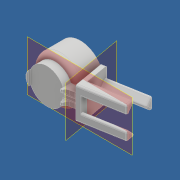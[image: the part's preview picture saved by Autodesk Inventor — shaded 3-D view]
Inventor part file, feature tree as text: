
AUTODESK INVENTOR PART (.ipt)
format: ipt  version: 2017 (Build 210142000, 142)  size: 999,424 bytes
history: native  units: mm
features: fillet x50, sketch x17, extrude x15, projected_geometry x11, chamfer x10, revolve x2, thicken_offset x2, plane x2
ambient origin geometry x8: Origin, YZ Plane, XZ Plane, XY Plane, X Axis, Y Axis, Z Axis, Center Point
bodies: Solid1 (feature_tree)
feature tree (109):
  revolve  "Revolution1"  [1 undecoded]
  extrude  "Extrusion1"  Depth=2.489174mm
  extrude  "Extrusion2"  Depth=5.0mm
  extrude  "Extrusion3"  Depth=1.5mm
  extrude  "Extrusion4"  Depth=1.5mm
  extrude  "Extrusion5"  Depth=1.5mm
  chamfer  "Chamfer1"  Distance=5.0mm
  chamfer  "Chamfer2"  Distance=82.0mm
  chamfer  "Chamfer3"  Distance=82.0mm
  chamfer  "Chamfer4"  Distance=10.0mm
  chamfer  "Chamfer5"  Distance=1.5mm
  chamfer  "Chamfer6"  Angle=45.0deg  [1 undecoded]
  chamfer  "Chamfer9"  Distance=14.6mm
  chamfer  "Chamfer10"  Distance=14.6mm
  chamfer  "Chamfer11"  Distance=7.25mm
  chamfer  "Chamfer12"  Distance=8.0mm Angle=45.0deg
  fillet  "Fillet1"  Radius=8.0mm
  fillet  "Fillet2"  Radius=8.0mm
  fillet  "Fillet3"  Radius=8.0mm
  fillet  "Fillet4"  Radius=5.0mm
  fillet  "Fillet5"  Radius=5.0mm
  fillet  "Fillet6"  Radius=5.0mm
  fillet  "Fillet7"  Radius=5.0mm
  fillet  "Fillet8"  Radius=5.0mm
  fillet  "Fillet11"  Radius=5.0mm
  fillet  "Fillet12"  Radius=2.0mm
  fillet  "Fillet13"  Radius=10.0mm
  fillet  "Fillet14"  Radius=1.0mm
  fillet  "Fillet15"  Radius=1.0mm
  fillet  "Fillet16"  Radius=1.0mm
  fillet  "Fillet17"  Radius=1.0mm
  fillet  "Fillet26"  Radius=1.0mm
  fillet  "Fillet30"  Radius=1.0mm
  extrude  "Extrusion7"  Depth=10.0mm
  extrude  "Extrusion8"  Depth=10.0mm
  fillet  "Fillet34"  Radius=10.0mm
  fillet  "Fillet35"  Radius=3.0mm
  revolve  "Revolution2"  [1 undecoded]
  extrude  "Extrusion9"  Depth=4.0mm
  extrude  "Extrusion10"  Depth=4.0mm
  fillet  "Fillet36"  Radius=1.0mm
  fillet  "Fillet37"  Radius=10.0mm
  extrude  "Extrusion11"  Depth=4.0mm TaperAngle=0.0deg
  extrude  "Extrusion12"  Depth=4.0mm
  extrude  "Extrusion14"  Depth=4.0mm
  extrude  "Extrusion15"  Depth=4.0mm
  thicken_offset  "Thicken1"
  thicken_offset  "Thicken2"
  fillet  "Fillet43"  Radius=5.0mm
  fillet  "Fillet44"  Radius=5.0mm
  fillet  "Fillet45"  Radius=5.0mm
  fillet  "Fillet46"  Radius=5.0mm
  extrude  "Extrusion16"  Depth=4.0mm
  fillet  "Fillet47"  Radius=1.745329mm
  fillet  "Fillet48"  Radius=30.0mm
  fillet  "Fillet49"  Radius=4.75mm
  fillet  "Fillet50"  Radius=10.0mm
  fillet  "Fillet51"  Radius=10.0mm
  fillet  "Fillet52"  Radius=8.0mm
  fillet  "Fillet53"  Radius=30.0mm
  fillet  "Fillet54"  Radius=17.0mm
  fillet  "Fillet55"  Radius=4.5mm
  fillet  "Fillet56"  Radius=1.5mm
  fillet  "Fillet57"  Radius=1.5mm
  fillet  "Fillet58"  Radius=5.5mm
  plane  "Work Plane1"
  extrude  "Extrusion17"  Depth=4.0mm TaperAngle=0.0deg
  fillet  "Fillet59"  Radius=4.0mm
  plane  "Work Plane2"
  fillet  "Fillet60"  Radius=11.7mm
  fillet  "Fillet61"  Radius=5.0mm
  fillet  "Fillet62"  Radius=5.0mm
  fillet  "Fillet63"  Radius=5.0mm
  fillet  "Fillet64"  Radius=5.0mm
  fillet  "Fillet65"  Radius=30.0mm
  fillet  "Fillet66"  Radius=38.1mm
  fillet  "Fillet67"  [1 undecoded]
  fillet  "Fillet68"  [1 undecoded]
  fillet  "Fillet69"  Radius=75.0mm
  fillet  "Fillet70"  Radius=30.696949mm
  fillet  "Fillet71"  Radius=3.0mm
  sketch  "Sketch1"  dims[d0=3.0mm d1=43.0mm]
  sketch  "Sketch2"  dims[d3=43.0mm d4=2.489174mm]
  sketch  "Sketch4"  dims[d5=45.0deg d6=5.0mm]
  sketch  "Sketch5"  dims[d7=90.0deg d8=1.5mm]
  projected_geometry  "Projected Loop1"
  sketch  "Sketch6"  dims[d9=1.5mm d10=1.5mm]
  sketch  "Sketch7"  dims[d11=1.5mm d12=1.5mm]
  sketch  "Sketch10"  dims[d13=1.5mm]
  sketch  "Sketch11"  dims[d14=1.5mm]
  sketch  "Sketch12"  dims[d15=1.5mm]
  projected_geometry  "Projected Loop2"
  projected_geometry  "Projected Loop3"
  sketch  "Sketch15"  dims[d18=40.0mm]
  projected_geometry  "Projected Loop6"
  projected_geometry  "Projected Loop7"
  sketch  "Sketch16"  dims[d19=40.0mm]
  projected_geometry  "Projected Loop8"
  projected_geometry  "Projected Loop9"
  projected_geometry  "Projected Loop10"
  projected_geometry  "Projected Loop11"
  sketch  "Sketch18"  dims[d20=40.0mm]
  projected_geometry  "Projected Loop13"
  sketch  "Sketch19"  dims[d21=40.0mm d22=5.0mm d23=0.0mm d24=82.0mm d25=0.0mm d26=82.0mm d27=0.0mm]
  sketch  "Sketch20"  dims[d28=17.5mm]
  sketch  "Sketch21"  dims[d29=21.0mm d30=10.0mm d31=0.0mm]
  sketch  "Sketch22"  dims[d32=7.3mm]
  sketch  "Sketch23"  dims[d33=7.3mm d34=1.5mm d35=45.0deg d36=14.6mm d37=14.6mm d38=7.25mm d39=0.0mm d40=8.0mm d41=2.0mm d42=45.0deg d43=8.0mm d44=2.0mm d45=45.0deg d46=8.0mm d47=2.0mm d48=45.0deg d49=8.0mm d50=2.0mm d51=45.0deg d52=5.0mm d53=1.0mm d54=45.0deg d55=5.0mm d56=1.0mm d57=45.0deg d64=5.0mm d65=1.0mm d66=45.0deg d67=5.0mm d68=1.0mm d69=45.0deg d70=5.0mm d71=1.0mm d72=45.0deg d73=5.0mm d74=1.0mm d75=45.0deg d76=2.0mm d77=10.0mm d78=1.0mm d79=1.0mm d80=1.0mm d81=1.0mm d82=1.0mm d83=1.0mm d86=10.0mm d87=10.0mm d88=10.0mm d89=3.0mm d90=3.0mm d91=3.0mm d92=3.0mm d101=1.0mm d108=10.0mm d109=15.0mm d110=0.0mm d112=60.5mm d113=5.0mm d114=5.0mm d115=5.0mm d116=5.0mm d117=5.0mm d118=0.0mm d121=5.0mm d122=5.0mm d123=1.745329mm d124=30.0mm d125=0.0mm d126=4.75mm d127=0.0mm d128=10.0mm d129=10.0mm d130=8.0mm d131=30.0mm d132=17.0mm d133=43.375mm d134=0.0mm d135=0.0mm d136=4.5mm d137=0.0mm d140=1.5mm d141=1.5mm d147=5.5mm d148=0.0mm d149=3.5mm d150=0.0mm d151=11.7mm d152=4.0mm d153=11.7mm d154=20.0mm d155=5.0mm d156=5.0mm d157=5.0mm d158=5.0mm d167=30.0mm d169=38.1mm d170=45.0deg d171=45.0deg d173=75.0mm d174=0.0mm d176=30.696949mm d177=3.0mm d178=3.0mm d179=3.0mm d180=3.0mm d181=3.0mm d182=3.0mm d183=3.0mm d184=3.0mm d185=3.0mm d186=3.0mm d187=3.0mm d188=3.0mm d189=17.0mm d190=2.75mm d191=20.0mm d192=0.0mm d193=0.0mm d194=2.0mm d195=2.0mm d196=2.0mm d197=2.0mm d198=2.0mm d199=2.0mm d200=2.0mm d201=2.0mm d202=2.0mm d203=4.0mm d204=4.0mm d205=4.0mm d206=4.0mm]
  projected_geometry  "Project Cut Edges1"
note: 5 required parameter values undecoded (feature->parameter linkage not recoverable at this tier; creation-order binding heuristic only, values carry confidence <= 0.55)